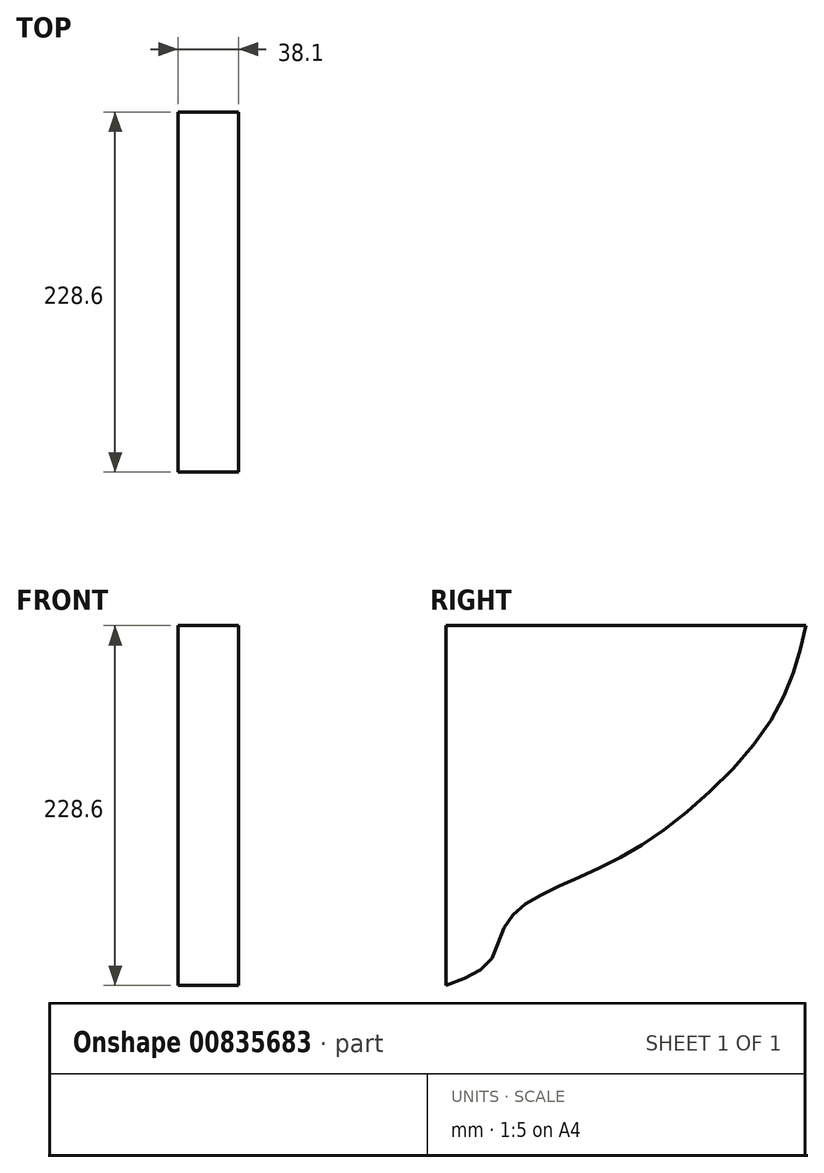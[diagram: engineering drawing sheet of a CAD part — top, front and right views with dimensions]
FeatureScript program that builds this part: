
annotation { "Feature Type Name" : "Feature", "Feature Type Description" : "" }
export const myFeature = defineFeature(function(context is Context, id is Id, definition is map)
    precondition{}
    {
        {
            var Q0;
            Q0=qCreatedBy(makeId("Right.planeOp"),FACE);
            var sketch = newSketch(context, id + "F0", { "sketchPlane" : qUnion([Q0])});
            skLineSegment(sketch, "E0", {"start": v(0, 0) * mm, "end": v(0, 228.6) * mm});
            skLineSegment(sketch, "E1", {"start": v(0, 228.6) * mm, "end": v(228.6, 228.6) * mm});
            skFitSpline(sketch, "E2", {"points": [v(0, 0) * mm, v(27.53, 14.91) * mm, v(37.38, 37.88) * mm, v(57.06, 55.69) * mm, v(95.03, 73.5) * mm, v(147.06, 105.37) * mm, v(208.46, 171.93) * mm, v(228.6, 228.6) * mm], "startDerivative": vector(276.96, 97.1) * mm, "endDerivative": vector(79.42, 340.8) * mm});
            skSolve(sketch);
        }
        {
            var Q0;
            Q0 = qSketchRegion(id + "F0", true);
            extrude(context, id + "F1", {"entities" : qUnion([Q0]), "depth" : 38.1 * mm, "offsetDistance" : 25.4 * mm});
        }
    });
